# Revit family: V90.196.xxx
name_source: partatom
category: Möbelsysteme
revit_build: Autodesk Revit 2015 (Build: 20160512_1515(x64)
units: mm (PartAtom-declared; Revit-internal decimal feet)

## types (35) — shared parameters
Beschreibung = GS-tested safety storage cabinets for unrestricted storage of flammable hazardous materials in work areas in accordance with EN 14470-1 and TRGS 510 with a fire resistance of 90 (Type 90)
Cabinet depth = 860 mm  [stored 2.82152 ft]
Cabinet height = 1967 mm
Diff. pressure (Air change 10 times) = 5.0 Pa
Door width = 362 mm  [stored 1.18766 ft]
Hersteller = asecos GmbH
Price information = Price from spring 2018
Price information 2 = Prices are ex works and without taxes and shipping
Product video = https://www.youtube.com
Sticker position rb = 200 mm  [stored 0.656168 ft]
Typenbild = <Keine Auswahl>
URL = https://www.asecos.com

## per-type parameters (varying)
| type | 4 shelves left side | 4 shelves right side | 5 shelves left side | 5 shelves right side | Air change 10 times | Air duct distance 1 | Air duct distance 2 | Bestellnummer DACH | Body colour | Cabinet width | Distributed load | Door colour | Double door | Handle position | Kosten | Modell | Order No. Global | exhaust pos. 1 | exhaust pos. 2 | inner width |
| V90.196.045_0012 with 4 shelves, light grey | Ja | Nein | Nein | Nein | 1.4 L/s | 225 mm | 589 mm | 35034-001-35100 | RAL 7035 Light grey | 450 mm  [stored 1.47638 ft] | 5.70 kN/m² | RAL 7035 Light grey | Nein | 514 mm | 3598.5 $ | V90.196.045.VDAC:0012 with 4 shelves | 35034-001-35100 | 285 mm | 590 mm | 384 mm |
| V90.196.081_0013 with 5+5 shelves, stainless steel doors, anthracite grey body | Nein | Nein | Ja | Ja | 2.5 L/s | 293 mm | 400 mm  [stored 1.31234 ft] | 35086-051-35103 | RAL 7016 Anthracite grey | 820 mm | 5.02 kN/m² | Stainless Steel | Ja | 514 mm | 5179 $ | V90.196.081.VDAC:0013 with 5+5 shelves | 35086-051-35103 | 587 mm | 402 mm  [stored 1.3189 ft] | 755 mm |
| V90.196.081_0013 with 4+5 shelves, gentian blue doors, anthracite grey body | Ja | Nein | Nein | Ja | 2.5 L/s | 293 mm | 400 mm  [stored 1.31234 ft] | 35086-047-35104 | RAL 7016 Anthracite grey | 820 mm | 5.02 kN/m² | RAL 5010 Gentian Blue | Ja | 401 mm | 4950 $ | V90.196.081.VDAC:0013 with 4+5 shelves | 35086-047-35104 | 587 mm | 402 mm  [stored 1.3189 ft] | 755 mm |
| V90.196.081_0013 with 4+4 shelves, gentian blue doors, anthracite grey body | Ja | Ja | Nein | Nein | 2.5 L/s | 293 mm | 400 mm  [stored 1.31234 ft] | 35086-047-35102 | RAL 7016 Anthracite grey | 820 mm | 5.02 kN/m² | RAL 5010 Gentian Blue | Ja | 401 mm | 4917 $ | V90.196.081.VDAC:0013 with 4+4 shelves | 35086-047-35102 | 587 mm | 402 mm  [stored 1.3189 ft] | 755 mm |
| V90.196.081_0013 with 4+5 shelves, stainless steel doors, anthracite grey body | Ja | Nein | Nein | Ja | 2.5 L/s | 293 mm | 400 mm  [stored 1.31234 ft] | 35086-051-35104 | RAL 7016 Anthracite grey | 820 mm | 5.02 kN/m² | Stainless Steel | Ja | 401 mm | 5146 $ | V90.196.081.VDAC:0013 with 4+5 shelves | 35086-051-35104 | 587 mm | 402 mm  [stored 1.3189 ft] | 755 mm |
| V90.196.045_0013 with 5 shelves, stainless steel door, anthracite body | Nein | Nein | Ja | Nein | 1.4 L/s | 225 mm | 589 mm | 35085-051-35101 | RAL 7016 Anthracite grey | 450 mm  [stored 1.47638 ft] | 5.70 kN/m² | Stainless Steel | Nein | 401 mm | 3729.5 $ | V90.196.045.VDAC:0013 with 5 shelves | 35085-051-35101 | 285 mm | 590 mm | 384 mm |
| V90.196.081_0013 with 4+4 shelves, traffic red doors, anthracite grey body | Ja | Ja | Nein | Nein | 2.5 L/s | 293 mm | 400 mm  [stored 1.31234 ft] | 35086-046-35102 | RAL 7016 Anthracite grey | 820 mm | 5.02 kN/m² | RAL 3020 Traffic Red | Ja | 401 mm | 4917 $ | V90.196.081.VDAC:0013 with 4+4 shelves | 35086-046-35102 | 587 mm | 402 mm  [stored 1.3189 ft] | 755 mm |
| V90.196.081_0013 with 5+5 shelves, gentian blue doors, anthracite grey body | Nein | Nein | Ja | Ja | 2.5 L/s | 293 mm | 400 mm  [stored 1.31234 ft] | 35086-047-35103 | RAL 7016 Anthracite grey | 820 mm | 5.02 kN/m² | RAL 5010 Gentian Blue | Ja | 401 mm | 4983 $ | V90.196.081.VDAC:0013 with 5+5 shelves | 35086-047-35103 | 587 mm | 402 mm  [stored 1.3189 ft] | 755 mm |
| V90.196.045_0013 with 4 shelves, gentian blue door, anthracite body | Ja | Nein | Nein | Nein | 1.4 L/s | 225 mm | 589 mm | 35085-047-35100 | RAL 7016 Anthracite grey | 450 mm  [stored 1.47638 ft] | 5.70 kN/m² | RAL 5010 Gentian Blue | Nein | 401 mm | 3598.5 $ | V90.196.045.VDAC:0013 with 4 shelves | 35085-047-35100 | 285 mm | 590 mm | 384 mm |
| V90.196.045_0013 with 4 shelves, stainless steel door, anthracite body | Ja | Nein | Nein | Nein | 1.4 L/s | 225 mm | 589 mm | 35085-051-35100 | RAL 7016 Anthracite grey | 450 mm  [stored 1.47638 ft] | 5.70 kN/m² | Stainless Steel | Nein | 401 mm | 3696.5 $ | V90.196.045.VDAC:0013 with 4 shelves | 35085-051-35100 | 285 mm | 590 mm | 384 mm |
| V90.196.045_0013 with 5 shelves, gentian blue door, anthracite body | Nein | Nein | Ja | Nein | 1.4 L/s | 225 mm | 589 mm | 35085-047-35101 | RAL 7016 Anthracite grey | 450 mm  [stored 1.47638 ft] | 5.70 kN/m² | RAL 5010 Gentian Blue | Nein | 401 mm | 3631.5 $ | V90.196.045.VDAC:0013 with 5 shelves | 35085-047-35101 | 285 mm | 590 mm | 384 mm |
| V90.196.045_0013 with 5 shelves, light grey door, anthracite body | Nein | Nein | Ja | Nein | 1.4 L/s | 225 mm | 589 mm | 35085-041-35101 | RAL 7016 Anthracite grey | 450 mm  [stored 1.47638 ft] | 5.70 kN/m² | RAL 7035 Light grey | Nein | 551 mm | 3631.5 $ | V90.196.045.VDAC:0013 with 5 shelves | 35085-041-35101 | 285 mm | 590 mm | 384 mm |
| V90.196.045_0013 with 5 shelves, traffic red door, anthracite body | Nein | Nein | Ja | Nein | 1.4 L/s | 225 mm | 589 mm | 35085-046-35101 | RAL 7016 Anthracite grey | 450 mm  [stored 1.47638 ft] | 5.70 kN/m² | RAL 3020 Traffic Red | Nein | 551 mm | 3631.5 $ | V90.196.045.VDAC:0013 with 5 shelves | 35085-046-35101 | 285 mm | 590 mm | 384 mm |
| V90.196.045_0013 with 4 shelves, traffic red door, anthracite body | Ja | Nein | Nein | Nein | 1.4 L/s | 225 mm | 589 mm | 35085-046-35100 | RAL 7016 Anthracite grey | 450 mm  [stored 1.47638 ft] | 5.70 kN/m² | RAL 3020 Traffic Red | Nein | 551 mm | 3598.5 $ | V90.196.045.VDAC:0013 with 4 shelves | 35085-046-35100 | 285 mm | 590 mm | 384 mm |
| V90.196.045_0013 with 4 shelves, warning yellow door, anthracite body | Ja | Nein | Nein | Nein | 1.4 L/s | 225 mm | 589 mm | 35085-040-35100 | RAL 7016 Anthracite grey | 450 mm  [stored 1.47638 ft] | 5.70 kN/m² | RAL 1004 warning yellow | Nein | 551 mm | 3598.5 $ | V90.196.045.VDAC:0013 with 4 shelves | 35085-040-35100 | 285 mm | 590 mm | 384 mm |
| V90.196.045_0013 with 4 shelves, light grey door, anthracite body | Ja | Nein | Nein | Nein | 1.4 L/s | 225 mm | 589 mm | 35085-041-35100 | RAL 7016 Anthracite grey | 450 mm  [stored 1.47638 ft] | 5.70 kN/m² | RAL 7035 Light grey | Nein | 551 mm | 3598.5 $ | V90.196.045.VDAC:0013 with 4 shelves | 35085-041-35100 | 285 mm | 590 mm | 384 mm |
| V90.196.045_0013 with 5 shelves, warning yellow door, anthracite body | Nein | Nein | Ja | Nein | 1.4 L/s | 225 mm | 589 mm | 35085-040-35101 | RAL 7016 Anthracite grey | 450 mm  [stored 1.47638 ft] | 5.70 kN/m² | RAL 1004 warning yellow | Nein | 551 mm | 3631.5 $ | V90.196.045.VDAC:0013 with 5 shelves | 35085-040-35101 | 285 mm | 590 mm | 384 mm |
| V90.196.045_0012 with 5 shelves, light grey | Nein | Nein | Ja | Nein | 1.4 L/s | 225 mm | 589 mm | 35034-001-35101 | RAL 7035 Light grey | 450 mm  [stored 1.47638 ft] | 5.70 kN/m² | RAL 7035 Light grey | Nein | 551 mm | 3631.5 $ | V90.196.045.VDAC:0012 with 5 shelves | 35034-001-35101 | 285 mm | 590 mm | 384 mm |
| V90.196.045_0012 with 5 shelves, pure white | Nein | Nein | Ja | Nein | 1.4 L/s | 225 mm | 589 mm | 35034-005-35101 | RAL 9010 Pure white | 450 mm  [stored 1.47638 ft] | 5.70 kN/m² | RAL 9010 Pure white | Nein | 551 mm | 3631.5 $ | V90.196.045.VDAC:0012 with 5 shelves | 35034-005-35101 | 285 mm | 590 mm | 384 mm |
| V90.196.045_0012 with 4 shelves, pure white | Ja | Nein | Nein | Nein | 1.4 L/s | 225 mm | 589 mm | 35034-005-35100 | RAL 9010 Pure white | 450 mm  [stored 1.47638 ft] | 5.70 kN/m² | RAL 9010 Pure white | Nein | 551 mm | 3598.5 $ | V90.196.045.VDAC:0012 with 4 shelves | 35034-005-35100 | 285 mm | 590 mm | 384 mm |
| V90.196.081_0013 with 4+4 shelves, stainless steel doors, anthracite grey body | Ja | Ja | Nein | Nein | 2.5 L/s | 293 mm | 400 mm  [stored 1.31234 ft] | 35086-051-35102 | RAL 7016 Anthracite grey | 820 mm | 5.02 kN/m² | Stainless Steel | Ja | 514 mm | 5113 $ | V90.196.081.VDAC:0013 with 4+4 shelves | 35086-051-35102 | 587 mm | 402 mm  [stored 1.3189 ft] | 755 mm |
| V90.196.081_0013 with 4+5 shelves, traffic red doors, anthracite grey body | Ja | Nein | Nein | Ja | 2.5 L/s | 293 mm | 400 mm  [stored 1.31234 ft] | 35086-046-35104 | RAL 7016 Anthracite grey | 820 mm | 5.02 kN/m² | RAL 3020 Traffic Red | Ja | 401 mm | 4950 $ | V90.196.081.VDAC:0013 with 4+5 shelves | 35086-046-35104 | 587 mm | 402 mm  [stored 1.3189 ft] | 755 mm |
| V90.196.081_0013 with 5+5 shelves, traffic red doors, anthracite grey body | Nein | Nein | Ja | Ja | 2.5 L/s | 293 mm | 400 mm  [stored 1.31234 ft] | 35086-046-35103 | RAL 7016 Anthracite grey | 820 mm | 5.02 kN/m² | RAL 3020 Traffic Red | Ja | 401 mm | 4983 $ | V90.196.081.VDAC:0013 with 5+5 shelves | 35086-046-35103 | 587 mm | 402 mm  [stored 1.3189 ft] | 755 mm |
| V90.196.081_0013 with 4+4 shelves, light grey doors, anthracite grey body | Ja | Ja | Nein | Nein | 2.5 L/s | 293 mm | 400 mm  [stored 1.31234 ft] | 35086-041-35102 | RAL 7016 Anthracite grey | 820 mm | 5.02 kN/m² | RAL 7035 Light grey | Ja | 401 mm | 4917 $ | V90.196.081.VDAC:0013 with 4+4 shelves | 35086-041-35102 | 587 mm | 402 mm  [stored 1.3189 ft] | 755 mm |
| V90.196.081_0013 with 4+5 shelves, light grey doors, anthracite grey body | Ja | Nein | Nein | Ja | 2.5 L/s | 293 mm | 400 mm  [stored 1.31234 ft] | 35086-041-35104 | RAL 7016 Anthracite grey | 820 mm | 5.02 kN/m² | RAL 7035 Light grey | Ja | 401 mm | 4950 $ | V90.196.081.VDAC:0013 with 4+5 shelves | 35086-041-35104 | 587 mm | 402 mm  [stored 1.3189 ft] | 755 mm |
| V90.196.081_0013 with 5+5 shelves, light grey doors, anthracite grey body | Nein | Nein | Ja | Ja | 2.5 L/s | 293 mm | 400 mm  [stored 1.31234 ft] | 35086-041-35103 | RAL 7016 Anthracite grey | 820 mm | 5.02 kN/m² | RAL 7035 Light grey | Ja | 401 mm | 4983 $ | V90.196.081.VDAC:0013 with 5+5 shelves | 35086-041-35103 | 587 mm | 402 mm  [stored 1.3189 ft] | 755 mm |
| V90.196.081_0013 with 4+4 shelves, warning yellow doors, anthracite grey body | Ja | Ja | Nein | Nein | 2.5 L/s | 293 mm | 400 mm  [stored 1.31234 ft] | 35086-040-35102 | RAL 7016 Anthracite grey | 820 mm | 5.02 kN/m² | RAL 1004 warning yellow | Ja | 401 mm | 4917 $ | V90.196.081.VDAC:0013 with 4+4 shelves | 35086-040-35102 | 587 mm | 402 mm  [stored 1.3189 ft] | 755 mm |
| V90.196.081_0013 with 4+5 shelves, warning yellow doors, anthracite grey body | Ja | Nein | Nein | Ja | 2.5 L/s | 293 mm | 400 mm  [stored 1.31234 ft] | 35086-040-35104 | RAL 7016 Anthracite grey | 820 mm | 5.02 kN/m² | RAL 1004 warning yellow | Ja | 401 mm | 4950 $ | V90.196.081.VDAC:0013 with 4+5 shelves | 35086-040-35104 | 587 mm | 402 mm  [stored 1.3189 ft] | 755 mm |
| V90.196.081_0013 with 5+5 shelves, warning yellow doors, anthracite grey body | Nein | Nein | Ja | Ja | 2.5 L/s | 293 mm | 400 mm  [stored 1.31234 ft] | 35086-040-35103 | RAL 7016 Anthracite grey | 820 mm | 5.02 kN/m² | RAL 1004 warning yellow | Ja | 401 mm | 4983 $ | V90.196.081.VDAC:0013 with 5+5 shelves | 35086-040-35103 | 587 mm | 402 mm  [stored 1.3189 ft] | 755 mm |
| V90.196.081_0012 with 4+4 shelves, pure white | Ja | Ja | Nein | Nein | 2.5 L/s | 293 mm | 400 mm  [stored 1.31234 ft] | 35035-005-35102 | RAL 9010 Pure white | 820 mm | 5.02 kN/m² | RAL 9010 Pure white | Ja | 401 mm | 4917 $ | V90.196.081.VDAC:0012 with 4+4 shelves | 35035-005-35102 | 587 mm | 300 mm | 755 mm |
| V90.196.081_0012 with 4+5 shelves, pure white | Ja | Nein | Nein | Ja | 2.5 L/s | 293 mm | 400 mm  [stored 1.31234 ft] | 35035-005-35104 | RAL 9010 Pure white | 820 mm | 5.02 kN/m² | RAL 9010 Pure white | Ja | 401 mm | 4950 $ | V90.196.081.VDAC:0012 with 4+5 shelves | 35035-005-35104 | 587 mm | 300 mm | 755 mm |
| V90.196.081_0012 with 5+5 shelves, pure white | Nein | Nein | Ja | Ja | 2.5 L/s | 293 mm | 400 mm  [stored 1.31234 ft] | 35035-005-35103 | RAL 9010 Pure white | 820 mm | 5.02 kN/m² | RAL 9010 Pure white | Ja | 401 mm | 4983 $ | V90.196.081.VDAC:0012 with 5+5 shelves | 35035-005-35103 | 587 mm | 300 mm | 755 mm |
| V90.196.081_0012 with 4+4 shelves, light grey | Ja | Ja | Nein | Nein | 2.5 L/s | 293 mm | 400 mm  [stored 1.31234 ft] | 35035-001-35102 | RAL 7035 Light grey | 820 mm | 5.02 kN/m² | RAL 7035 Light grey | Ja | 401 mm | 4917 $ | V90.196.081.VDAC:0012 with 4+4 shelves | 35035-001-35102 | 587 mm | 300 mm | 755 mm |
| V90.196.081_0012 with 4+5 shelves, light grey | Ja | Nein | Nein | Ja | 2.5 L/s | 293 mm | 400 mm  [stored 1.31234 ft] | 35035-001-35104 | RAL 7035 Light grey | 820 mm | 5.02 kN/m² | RAL 7035 Light grey | Ja | 401 mm | 4950 $ | V90.196.081.VDAC:0012 with 4+5 shelves | 35035-001-35104 | 587 mm | 300 mm | 755 mm |
| V90.196.081_0012 with 5+5 shelves, light grey | Nein | Nein | Ja | Ja | 2.5 L/s | 293 mm | 400 mm  [stored 1.31234 ft] | 35035-001-35103 | RAL 7035 Light grey | 820 mm | 5.02 kN/m² | RAL 7035 Light grey | Ja | 401 mm | 4983 $ | V90.196.081.VDAC:0012 with 5+5 shelves | 35035-001-35103 | 587 mm | 300 mm | 755 mm |

note: [stored X ft] marks values corroborated as IEEE doubles in the binary element streams (Revit-internal decimal feet)
